# Revit family: Atdec-Wall_Mount_Rail-VFL-
name_source: partatom
category: Generic Models
revit_build: Autodesk Revit 2016 (Build: 20150220_1215(x64)
units: mm (PartAtom-declared; Revit-internal decimal feet)

## family parameters
Can host rebar = No
Cut with Voids When Loaded = No
Host = Face
Part Type = Normal
Room Calculation Point = No
Round Connector Dimension = Use Diameter
Shared = No

## types (1)
- TH-1040-VFL
    Assembly Code = E1010800
    Colour Options = Black
    Default Elevation = 1219 mm
    Description = Slim full motion mount
    Flat Screen maximum supported weight, kg = 35kg (77lb)
    Manufacturer = Atdec
    Master Carton Dimensions = 400mm (15.7") Lenght, 370mm (13") Width, 370mm (14.5") Height
    Material = Steel
    Maximum distance from wall (mm) = 506mm (19.92")
    Minimum distance from wall (mm) = 52mm (2.05")
    Model = TH-1040-VFL
    Pan adjustment = 90° left and 90° right
    Product Family = Wall Mount Rail
    Product Information = https://www.atdec.com.au
    Range of movement = Full Motion
    Security feature = -
    Single Unit Dimensions = 387mm (15.2") Lenght, 317mm (12.5") Width, 58mm (2.3") Height
    Single units per master pack = 6
    Tilt Adjustment = 10° of downward tilt
    UPC Code = 881493007666
    URL = www.atdec.com.au
    Universal Height (mm) = -
    Universal Width (mm) = -
    VESA mounting hole pattern, mm = 100x100, 100x150, 200x100, 200x200
    Warranty = 10 years
    Weight, master carton = 23.3kg (51.3lb)
    Weight, single unit = 3.2kg (7lb)
    Width = 500 mm

## geometry (parser evidence)
native form markers: Sweep x10
no freeform markers — native parametric forms only
